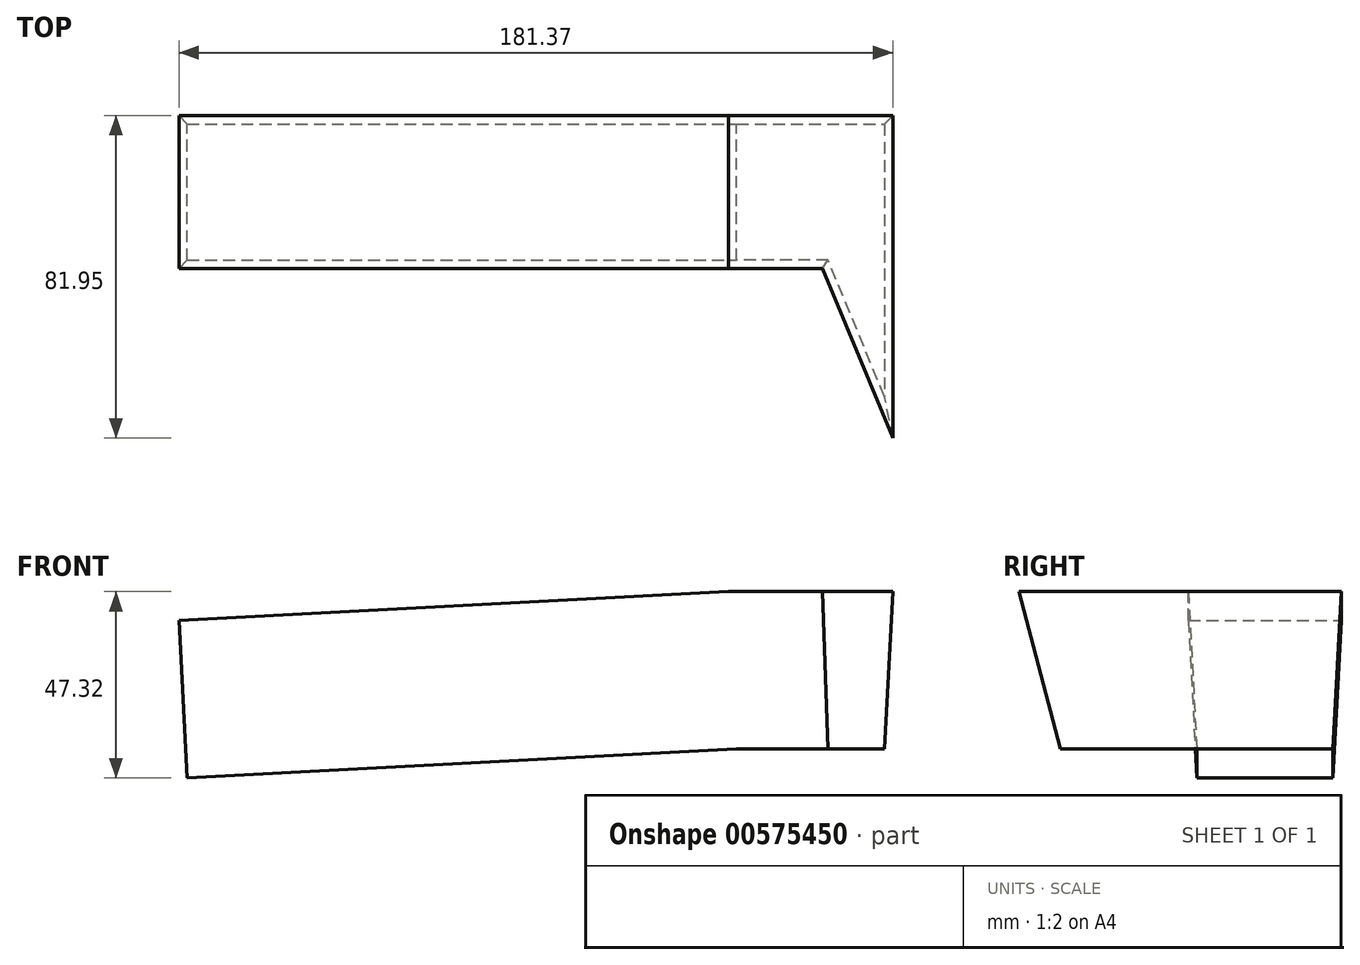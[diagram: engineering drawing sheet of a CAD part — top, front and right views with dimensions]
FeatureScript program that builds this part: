
annotation { "Feature Type Name" : "Feature", "Feature Type Description" : "" }
export const myFeature = defineFeature(function(context is Context, id is Id, definition is map)
    precondition{}
    {
        {
            var Q0;
            Q0=qCreatedBy(makeId("Top.planeOp"),FACE);
            var sketch = newSketch(context, id + "F0", { "sketchPlane" : qUnion([Q0])});
            skLineSegment(sketch, "E0", {"start": v(-26.14, 74.06) * mm, "end": v(-26.14, 4.77) * mm});
            skLineSegment(sketch, "E1", {"start": v(-26.14, 4.77) * mm, "end": v(-40.45, 39.42) * mm});
            skPoint(sketch, "E1.endSnap0", {"position": v(-26.14, 39.42) * mm});
            skLineSegment(sketch, "E2", {"start": v(-40.45, 39.42) * mm, "end": v(-63.69, 39.42) * mm});
            skLineSegment(sketch, "E3", {"start": v(-63.69, 39.42) * mm, "end": v(-63.69, 74.06) * mm});
            skLineSegment(sketch, "E4", {"start": v(-63.69, 74.06) * mm, "end": v(-26.14, 74.06) * mm});
            skSolve(sketch);
        }
        {
            var Q0;
            Q0=qCreatedBy(makeId("Top.planeOp"),FACE);
            var sketch = newSketch(context, id + "F1", { "sketchPlane" : qUnion([Q0])});
            skSolve(sketch);
        }
        {
            var Q0;
            Q0 = qSketchRegion(id + "F1", true);
            var Q1;
            Q1=makeQuery(id+"F0.imprint","IMPRINT",FACE,{"disambiguationData":[TD([[makeQuery(id+"F0.imprint","IMPRINT",EDGE,{"derivedFrom":sQuery(id+"F0.wireOp",EDGE,"E0")}),-1.0]])]});
            extrude(context, id + "F2", {"entities" : qUnion([Q0, Q1]), "depth" : 40 * mm, "offsetDistance" : 25.4 * mm, "hasDraft" : true, "draftAngle" : 3 * degree});
        }
        {
            var Q0;
            Q0=makeQuery(id+"F2.opExtrude","SWEPT_FACE",FACE,{"disambiguationData":[OSD([sQuery(id+"F0.wireOp",EDGE,"E3")])]});
            extrude(context, id + "F3", {"entities" : qUnion([Q0]), "operationType" : NewBodyOperationType.ADD, "depth" : 139.82 * mm, "offsetDistance" : 25.4 * mm});
        }
    });
